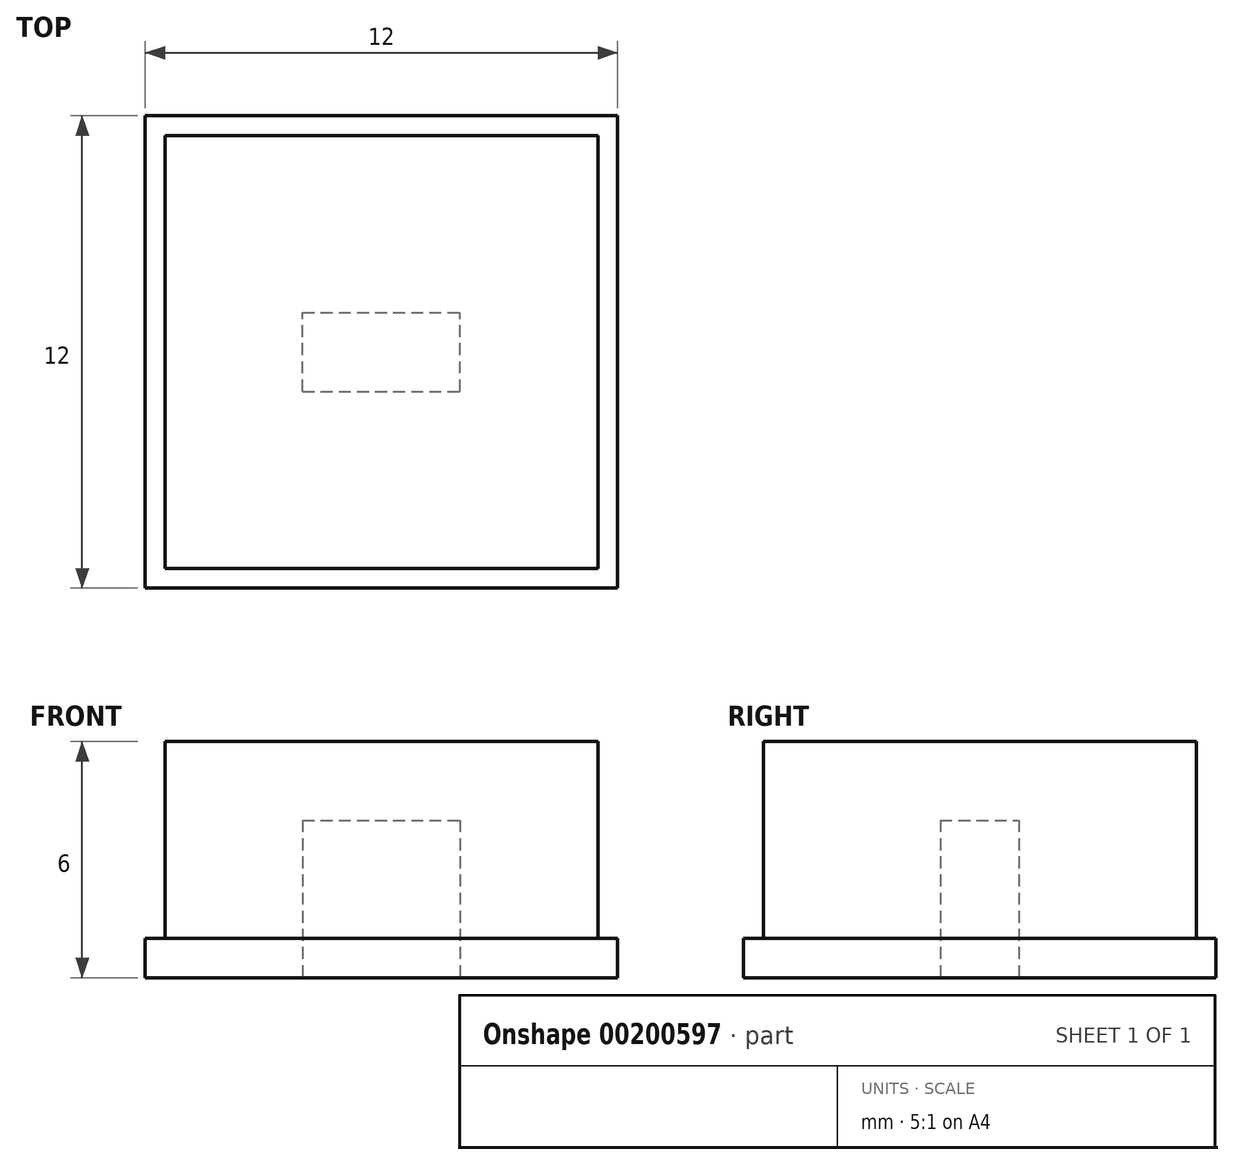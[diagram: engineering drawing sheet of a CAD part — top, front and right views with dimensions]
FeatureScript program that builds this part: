
annotation { "Feature Type Name" : "Feature", "Feature Type Description" : "" }
export const myFeature = defineFeature(function(context is Context, id is Id, definition is map)
    precondition{}
    {
        {
            var Q0;
            Q0=qCreatedBy(makeId("Top.planeOp"),FACE);
            var sketch = newSketch(context, id + "F0", { "sketchPlane" : qUnion([Q0])});
            skLineSegment(sketch, "E0.bottom", {"start": v(-6, 6) * mm, "end": v(6, 6) * mm});
            skLineSegment(sketch, "E0.top", {"start": v(-6, -6) * mm, "end": v(6, -6) * mm});
            skLineSegment(sketch, "E0.left", {"start": v(-6, 6) * mm, "end": v(-6, -6) * mm});
            skLineSegment(sketch, "E0.right", {"start": v(6, 6) * mm, "end": v(6, -6) * mm});
            skPoint(sketch, "E0.middle", {"position": v(0, 0) * mm});
            skSolve(sketch);
        }
        {
            var Q0;
            Q0=makeQuery(id+"F0.imprint","IMPRINT",FACE,{"disambiguationData":[TD([[makeQuery(id+"F0.imprint","IMPRINT",EDGE,{"derivedFrom":sQuery(id+"F0.wireOp",EDGE,"E0.bottom")}),-1.0]])]});
            var sketch = newSketch(context, id + "F1", { "sketchPlane" : qUnion([Q0])});
            skLineSegment(sketch, "E1.bottom", {"start": v(-5.5, 5.5) * mm, "end": v(5.5, 5.5) * mm});
            skLineSegment(sketch, "E1.top", {"start": v(-5.5, -5.5) * mm, "end": v(5.5, -5.5) * mm});
            skLineSegment(sketch, "E1.left", {"start": v(-5.5, 5.5) * mm, "end": v(-5.5, -5.5) * mm});
            skLineSegment(sketch, "E1.right", {"start": v(5.5, 5.5) * mm, "end": v(5.5, -5.5) * mm});
            skPoint(sketch, "E1.middle", {"position": v(0, 0) * mm});
            skSolve(sketch);
        }
        {
            var Q0;
            Q0=makeQuery(id+"F1.imprint","IMPRINT",FACE,{"disambiguationData":[TD([[makeQuery(id+"F1.imprint","IMPRINT",EDGE,{"derivedFrom":sQuery(id+"F1.wireOp",EDGE,"E1.bottom")}),-1.0]])]});
            extrude(context, id + "F2", {"entities" : qUnion([Q0]), "depth" : 6 * mm});
        }
        {
            var Q0;
            Q0=makeQuery(id+"F0.imprint","IMPRINT",FACE,{"disambiguationData":[TD([[makeQuery(id+"F0.imprint","IMPRINT",EDGE,{"derivedFrom":sQuery(id+"F0.wireOp",EDGE,"E0.bottom")}),-1.0]])]});
            extrude(context, id + "F3", {"entities" : qUnion([Q0]), "operationType" : NewBodyOperationType.ADD, "depth" : 1 * mm});
        }
        {
            var Q0;
            Q0=makeQuery(id+"F3.boolean.opBoolean","MERGE",FACE,{"derivedFrom":[makeQuery(id+"F2.opExtrude","CAP_FACE",FACE,{"disambiguationData":[OSD([sQuery(id+"F1.wireOp",EDGE,"E1.bottom"),sQuery(id+"F1.wireOp",EDGE,"E1.top"),sQuery(id+"F1.wireOp",EDGE,"E1.left"),sQuery(id+"F1.wireOp",EDGE,"E1.right")])],"isStart":true}),makeQuery(id+"F3.opExtrude","CAP_FACE",FACE,{"disambiguationData":[OSD([sQuery(id+"F0.wireOp",EDGE,"E0.bottom"),sQuery(id+"F0.wireOp",EDGE,"E0.top"),sQuery(id+"F0.wireOp",EDGE,"E0.left"),sQuery(id+"F0.wireOp",EDGE,"E0.right")])],"isStart":true})]});
            var sketch = newSketch(context, id + "F4", { "sketchPlane" : qUnion([Q0])});
            skLineSegment(sketch, "E2.bottom", {"start": v(-2, 1) * mm, "end": v(2, 1) * mm});
            skLineSegment(sketch, "E2.top", {"start": v(-2, -1) * mm, "end": v(2, -1) * mm});
            skLineSegment(sketch, "E2.left", {"start": v(-2, 1) * mm, "end": v(-2, -1) * mm});
            skLineSegment(sketch, "E2.right", {"start": v(2, 1) * mm, "end": v(2, -1) * mm});
            skPoint(sketch, "E2.middle", {"position": v(0, 0) * mm});
            skSolve(sketch);
        }
        {
            var Q0;
            Q0=makeQuery(id+"F4.imprint","IMPRINT",FACE,{"disambiguationData":[TD([[makeQuery(id+"F4.imprint","IMPRINT",EDGE,{"derivedFrom":sQuery(id+"F4.wireOp",EDGE,"E2.bottom")}),-1.0]])]});
            extrude(context, id + "F5", {"entities" : qUnion([Q0]), "operationType" : NewBodyOperationType.REMOVE, "oppositeDirection" : true, "depth" : 4 * mm});
        }
    });
